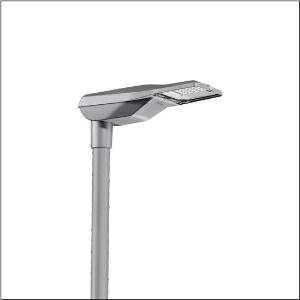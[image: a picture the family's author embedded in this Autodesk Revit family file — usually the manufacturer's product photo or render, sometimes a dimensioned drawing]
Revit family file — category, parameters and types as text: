
# Revit family: streetlight_sl_21_micro___st1_0a_5xe5d33a08db_1e00
name_source: partatom
category: Lighting Fixtures
units: mm (PartAtom-declared; Revit-internal decimal feet)

## family parameters
Cut with Voids When Loaded = No
Host = Face
Light Source = No
Part Type = Normal
Room Calculation Point = No
Round Connector Dimension = Use Diameter
Shared = No

## types (1)
- --- (1 x LED, 5110 lm, 39.1 W, 3000K)
    Apparent Load = 39 VA
    CIE Flux Codes = 37 72 97 100 100
    Color Rendering = 70
    Color Temperature = 3000K
    Default Elevation = 1800 mm
    Description = Streetlight SL 21 micro, mast luminaire, primary light control with lens, of PMMA, primary optical cover: cover, of toughened safety glass, transparent, light distribution: ST1.0a, light emission: direct distribution, primary light characteristic: asymmetric, installation type: side-entry, post-top, LED, 3G 1.5mm², High Power LED, rated luminous flux: 5.110lm, luminous efficacy: 131lm/W, light colour: 730, colour temperature: 3000K, control: flexible luminous flux parameterisation, time-dependent luminous flux control, constant luminous flux control, overheat protection, mains connection: 230..240V, AC, 50/60Hz, connection cable pre-assembled, cable length: 6,5m, wiring characteristics: H07RN-F, start of lifetime: 39W, end of service life: 41W, reduction: 18W, luminaire housing, of diecast aluminium, powder-coated, Siteco® metallic grey (DB 702S), corrosivity category C5 mid according to DIN EN ISO 12944, please order mast flange separately, inclination adjustable: 0°, 5°, 10°, 15°, sealing non-destructively replaceable, multi-level sealing system, length: 528mm, width: 235mm, height: 110mm, mast flange for spigot size: 42mm (side-entry): 5XC10008XM4, 60/48mm (side-entry/post-top): 5XC10108XM2, 76/60mm (side-entry/post-top): 5XC10108XM1, protection rating (complete): IP66, insulation class (complete): insulation class II (safety insulation), certification: CE, ENEC, ENEC+, VDE, impact resistance: IK09, permissible operating ambient temperature for outdoor applications: -40..+50°C, standard-compliant lighting for roads and squares, packaging unit: 1 piece

Light Distribution: ST1.0a
    Height = 110 mm
    Lamp = 1 x LED
    Lamp Light Flux = 5110 lm
    Lamp Power = 39.1 W
    Lamp count = 1
    Length = 528 mm
    Luminous efficacy = 131 lm/W
    Manufacturer = Siteco
    ModVariant = No
    Model = 5XE5D33A08DB
    Number of Poles = 1
    OnlyDefault = Yes
    Power Factor = 1
    Product Name = Streetlight SL 21 micro | ST1.0a
    Product group = mast luminaire | pylon top
    ProductGroupID = 6100
    Protection Class = Protection class II
    Protection Degree = IP 66
    RLX_Detail_Level = 1
    RLX_Emergency_Light_Flux = 0 lm
    RLX_Emergency_Type = 0
    RLX_Emergency_Type_DB = No
    RlxData = <blob elided: 98449 chars, md5=e1f828b1>
    Socket = socket
    Standby Power = 0 W
    System Light Flux = 5110 lm
    System Power = 39 W
    Type Comments = factory setting: luminous flux: 100 % | Output Level: 100 % | 765 mA
    Type Image = l_1006881.jpg
    URL = http://relux.com
    VarID = @adj_087933
    Voltage = 0 V
    Weight = 0.00 kg
    Width = 235 mm

## geometry (parser evidence)
native form markers: Blend x4, Sweep x10
no freeform markers — native parametric forms only
